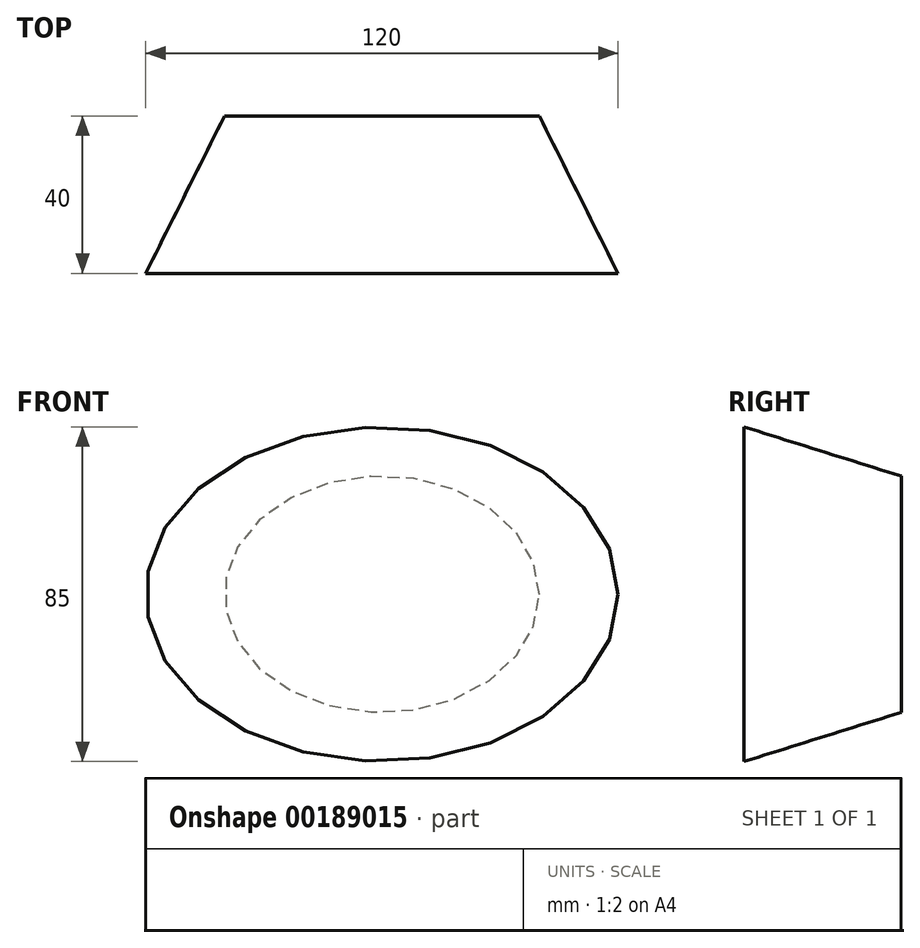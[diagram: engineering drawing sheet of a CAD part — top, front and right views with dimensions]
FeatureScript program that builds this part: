
annotation { "Feature Type Name" : "Feature", "Feature Type Description" : "" }
export const myFeature = defineFeature(function(context is Context, id is Id, definition is map)
    precondition{}
    {
        {
            var Q0;
            Q0=qCreatedBy(makeId("Front.planeOp"),FACE);
            var sketch = newSketch(context, id + "F0", { "sketchPlane" : qUnion([Q0])});
            skEllipse(sketch, "E0", {"center": v(0, 0) * mm, "majorRadius": 40 * mm, "minorRadius": 30 * mm, "majorAxis": v(1, 0)});
            skSolve(sketch);
        }
        {
            var Q0;
            Q0=qCreatedBy(makeId("Front.planeOp"),FACE);
            cPlane(context, id + "F1", {"entities" : qUnion([Q0]), "cplaneType" : CPlaneType.OFFSET, "offset" : 40 * mm, "width" : 150 * mm, "height" : 150 * mm});
        }
        {
            var Q0;
            Q0=qCreatedBy(id+"F1.planeOp",FACE);
            var sketch = newSketch(context, id + "F2", { "sketchPlane" : qUnion([Q0])});
            skEllipse(sketch, "E1", {"center": v(0, 0) * mm, "majorRadius": 60 * mm, "minorRadius": 42.5 * mm, "majorAxis": v(1, 0)});
            skSolve(sketch);
        }
        {
            var Q0;
            Q0=makeQuery(id+"F2.imprint","IMPRINT",FACE,{"disambiguationData":[TD([[makeQuery(id+"F2.imprint","IMPRINT",EDGE,{"derivedFrom":sQuery(id+"F2.wireOp",EDGE,"E1")}),1.0]])]});
            var Q1;
            Q1=makeQuery(id+"F0.imprint","IMPRINT",FACE,{"disambiguationData":[TD([[makeQuery(id+"F0.imprint","IMPRINT",EDGE,{"derivedFrom":sQuery(id+"F0.wireOp",EDGE,"E0")}),1.0]])]});
            loft(context, id + "F3", {"sheetProfilesArray" : [{ "sheetProfileEntities" : qUnion([Q0]) }, { "sheetProfileEntities" : qUnion([Q1]) }]});
        }
    });
